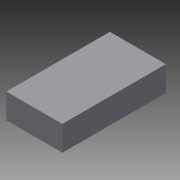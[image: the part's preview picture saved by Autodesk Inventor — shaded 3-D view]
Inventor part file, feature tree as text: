
AUTODESK INVENTOR PART (.ipt)
format: ipt  version: 2013 (Build 170138000, 138)  size: 186,880 bytes
history: native  units: in
note: dims shown in document units (in); Inventor stores cm internally (conversion verified against a paired STEP export)
features: extrude x3, sketch x3
ambient origin geometry x8: Origin, YZ Plane, XZ Plane, XY Plane, X Axis, Y Axis, Z Axis, Center Point
bodies: Solid1 (feature_tree)
feature tree (6):
  extrude  "Extrusion1"  Depth=2.0in
  extrude  "Extrusion2"  Depth=0.125in
  extrude  "Extrusion3"  Depth=0.875in
  sketch  "Sketch1"  dims[d0=4.5in d1=2.0in]
  sketch  "Sketch2"  dims[d2=8.3125in d3=0.0in d4=0.125in]
  sketch  "Sketch3"  dims[d5=0.3125in d6=0.875in d7=1.0in d8=0.0625in d9=0.3125in d10=0.0625in d11=0.3125in d12=0.0625in d13=0.3125in d14=0.0625in d15=0.3125in d16=0.0625in d17=0.3125in d18=0.0625in d19=0.0625in d21=0.0625in d23=0.0625in d24=0.3125in d25=0.0625in d26=0.3125in d27=0.3125in d28=0.625in d29=0.0in d30=0.25in d31=0.0in]
